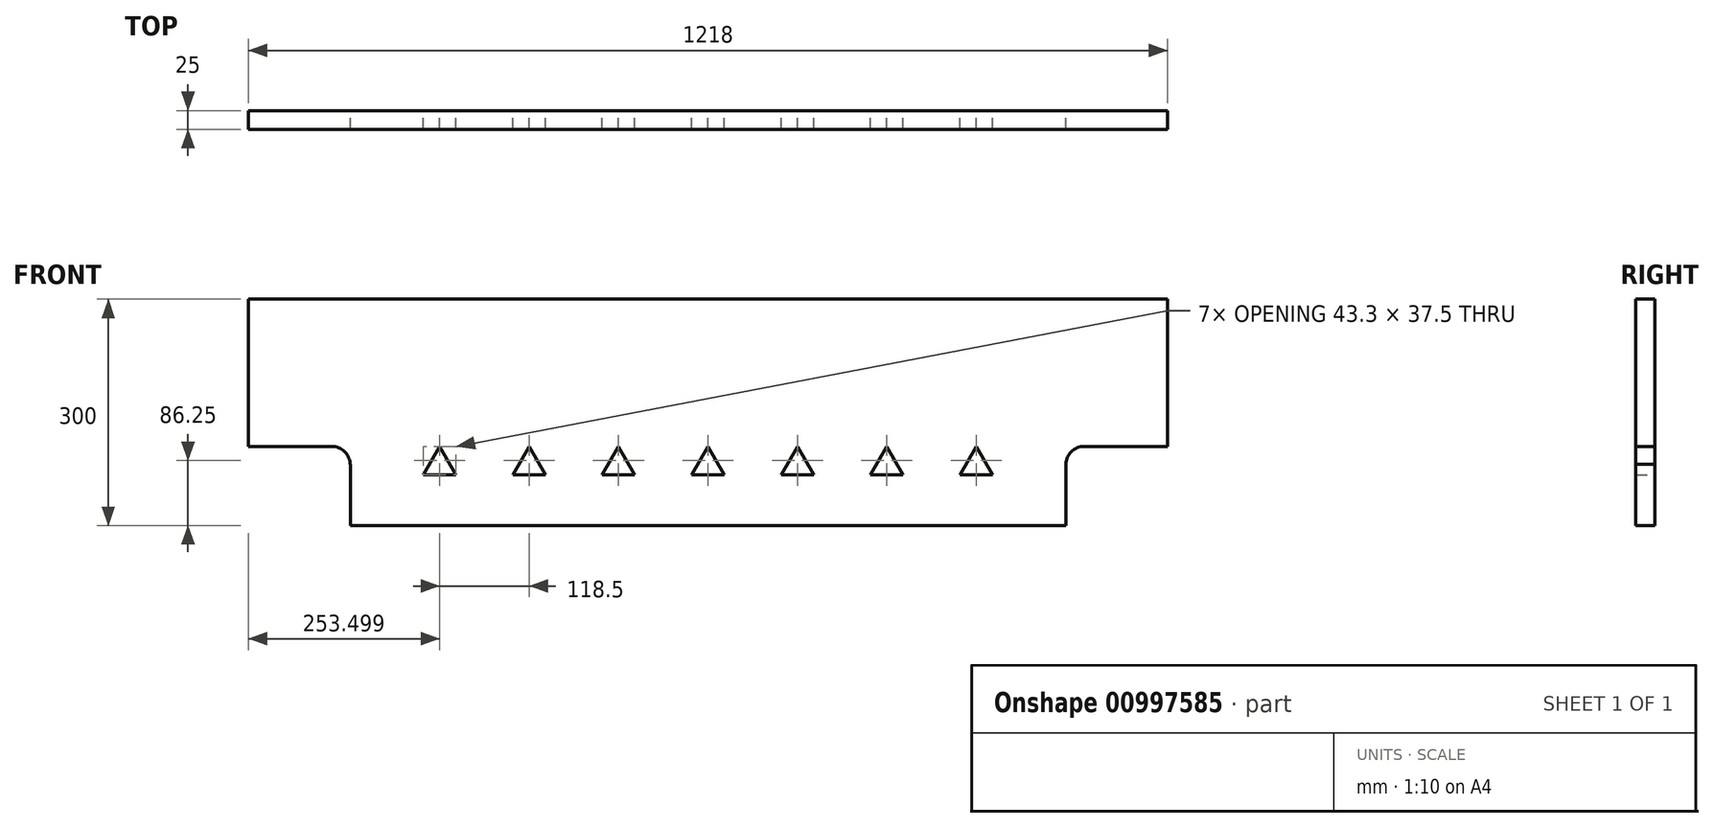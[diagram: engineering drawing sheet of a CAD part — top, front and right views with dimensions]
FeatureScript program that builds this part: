
annotation { "Feature Type Name" : "Feature", "Feature Type Description" : "" }
export const myFeature = defineFeature(function(context is Context, id is Id, definition is map)
    precondition{}
    {
        {
            var Q0;
            Q0=qCreatedBy(makeId("Front.planeOp"),FACE);
            var sketch = newSketch(context, id + "F0", { "sketchPlane" : qUnion([Q0])});
            skLineSegment(sketch, "E0.bottom", {"start": v(609, 150) * mm, "end": v(-609, 150) * mm});
            skLineSegment(sketch, "E0.left", {"start": v(609, 150) * mm, "end": v(609, -45) * mm});
            skLineSegment(sketch, "E0.right", {"start": v(-609, 150) * mm, "end": v(-609, -45) * mm});
            skPoint(sketch, "E0.middle", {"position": v(0, 0) * mm});
            skPoint(sketch, "E1.start.orphan", {"position": v(0, -150) * mm});
            skLineSegment(sketch, "E2", {"start": v(609, -45) * mm, "end": v(499, -45) * mm});
            skLineSegment(sketch, "E3", {"start": v(-609, -45) * mm, "end": v(-499, -45) * mm});
            skPoint(sketch, "E4.start.orphan", {"position": v(-100, -80) * mm});
            skPoint(sketch, "E5.orphan", {"position": v(609, -150) * mm});
            skPoint(sketch, "E6.orphan", {"position": v(-609, -150) * mm});
            skPoint(sketch, "E7.visualSharp", {"position": v(-474, -45) * mm});
            skArc(sketch, "E7.filletArc", {"start": v(-474, -70) * mm, "mid": v(-481.32, -52.32) * mm, "end": v(-499, -45) * mm});
            skPoint(sketch, "E8.visualSharp", {"position": v(474, -45) * mm});
            skArc(sketch, "E8.filletArc", {"start": v(499, -45) * mm, "mid": v(481.32, -52.32) * mm, "end": v(474, -70) * mm});
            skLineSegment(sketch, "E9.trimOffspring", {"start": v(-499, -45) * mm, "end": v(-609, -45) * mm});
            skPoint(sketch, "E10.trimOffspring.start.orphan", {"position": v(-100, -150) * mm});
            skLineSegment(sketch, "E11", {"start": v(-355.5, -45) * mm, "end": v(-355.5, -45.03) * mm});
            skLineSegment(sketch, "E12", {"start": v(-237, -45) * mm, "end": v(-237, -45.03) * mm});
            skLineSegment(sketch, "E13", {"start": v(-118.5, -45) * mm, "end": v(-118.5, -45.04) * mm});
            skLineSegment(sketch, "E14", {"start": v(0, -45) * mm, "end": v(0, -45.04) * mm});
            skLineSegment(sketch, "E15", {"start": v(237, -45) * mm, "end": v(237, -45.05) * mm});
            skLineSegment(sketch, "E16", {"start": v(355.5, -45) * mm, "end": v(355.5, -45.05) * mm});
            skLineSegment(sketch, "E17", {"start": v(-474, -70) * mm, "end": v(-474, -150) * mm});
            skLineSegment(sketch, "E18", {"start": v(-474, -150) * mm, "end": v(474.1, -150) * mm});
            skLineSegment(sketch, "E19", {"start": v(474.1, -150) * mm, "end": v(474.02, -68.93) * mm});
            skPoint(sketch, "E20.end.orphan", {"position": v(-474, -45.03) * mm});
            skCircle(sketch, "E21.cCircle", {"center": v(-355.5, -70) * mm, "radius": 25 * mm, "construction": true});
            skLineSegment(sketch, "E21.0", {"start": v(-355.5, -45) * mm, "end": v(-333.85, -82.5) * mm});
            skLineSegment(sketch, "E21.1", {"start": v(-333.85, -82.5) * mm, "end": v(-377.15, -82.5) * mm});
            skLineSegment(sketch, "E21.2", {"start": v(-377.15, -82.5) * mm, "end": v(-355.5, -45) * mm});
            skCircle(sketch, "E22.cCircle", {"center": v(-237, -70) * mm, "radius": 25 * mm, "construction": true});
            skLineSegment(sketch, "E22.0", {"start": v(-237, -45) * mm, "end": v(-215.35, -82.5) * mm});
            skLineSegment(sketch, "E22.1", {"start": v(-215.35, -82.5) * mm, "end": v(-258.65, -82.5) * mm});
            skLineSegment(sketch, "E22.2", {"start": v(-258.65, -82.5) * mm, "end": v(-237, -45) * mm});
            skCircle(sketch, "E23.cCircle", {"center": v(-118.5, -70) * mm, "radius": 25 * mm, "construction": true});
            skLineSegment(sketch, "E23.0", {"start": v(-118.5, -45) * mm, "end": v(-96.85, -82.5) * mm});
            skLineSegment(sketch, "E23.1", {"start": v(-96.85, -82.5) * mm, "end": v(-140.15, -82.5) * mm});
            skLineSegment(sketch, "E23.2", {"start": v(-140.15, -82.5) * mm, "end": v(-118.5, -45) * mm});
            skCircle(sketch, "E24.cCircle", {"center": v(0, -70) * mm, "radius": 25 * mm, "construction": true});
            skLineSegment(sketch, "E24.0", {"start": v(0, -45) * mm, "end": v(21.65, -82.5) * mm});
            skLineSegment(sketch, "E24.1", {"start": v(21.65, -82.5) * mm, "end": v(-21.65, -82.5) * mm});
            skLineSegment(sketch, "E24.2", {"start": v(-21.65, -82.5) * mm, "end": v(0, -45) * mm});
            skCircle(sketch, "E25.cCircle", {"center": v(118.5, -70) * mm, "radius": 25 * mm, "construction": true});
            skLineSegment(sketch, "E25.0", {"start": v(118.5, -45) * mm, "end": v(140.15, -82.5) * mm});
            skLineSegment(sketch, "E25.1", {"start": v(140.15, -82.5) * mm, "end": v(96.85, -82.5) * mm});
            skLineSegment(sketch, "E25.2", {"start": v(96.85, -82.5) * mm, "end": v(118.5, -45) * mm});
            skCircle(sketch, "E26.cCircle", {"center": v(237, -70) * mm, "radius": 25 * mm, "construction": true});
            skLineSegment(sketch, "E26.0", {"start": v(237, -45) * mm, "end": v(258.65, -82.5) * mm});
            skLineSegment(sketch, "E26.1", {"start": v(258.65, -82.5) * mm, "end": v(215.35, -82.5) * mm});
            skLineSegment(sketch, "E26.2", {"start": v(215.35, -82.5) * mm, "end": v(237, -45) * mm});
            skCircle(sketch, "E27.cCircle", {"center": v(355.5, -70) * mm, "radius": 25 * mm, "construction": true});
            skLineSegment(sketch, "E27.0", {"start": v(355.5, -45) * mm, "end": v(377.15, -82.5) * mm});
            skLineSegment(sketch, "E27.1", {"start": v(377.15, -82.5) * mm, "end": v(333.85, -82.5) * mm});
            skLineSegment(sketch, "E27.2", {"start": v(333.85, -82.5) * mm, "end": v(355.5, -45) * mm});
            skSolve(sketch);
        }
        {
            var Q0;
            Q0=makeQuery(id+"F0.imprint","IMPRINT",FACE,{"disambiguationData":[TD([[makeQuery(id+"F0.imprint","IMPRINT",EDGE,{"derivedFrom":sQuery(id+"F0.wireOp",EDGE,"E0.bottom")}),1.0]])]});
            var Q1;
            {var subQ0=sQuery(id+"F0.wireOp",EDGE,"1pv9D3iY-k3pF-b9IG-gRGy-6gTq31vdRF3B");Q1=makeQuery(id+"F0.imprint","IMPRINT",FACE,{"disambiguationData":[TD([[makeQuery(id+"F0.imprint","IMPRINT",EDGE,{"derivedFrom":subQ0}),-1.0]])]});}
            extrude(context, id + "F1", {"entities" : qUnion([Q0, Q1]), "depth" : 25 * mm, "offsetDistance" : 25 * mm});
        }
    });
